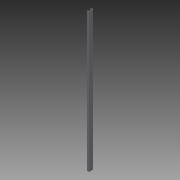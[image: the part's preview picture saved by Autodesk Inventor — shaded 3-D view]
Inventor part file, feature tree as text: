
AUTODESK INVENTOR PART (.ipt)
format: ipt  version: 2013 (Build 170138000, 138)  size: 72,192 bytes
history: native  units: in
note: dims shown in document units (in); Inventor stores cm internally (conversion verified against a paired STEP export)
features: extrude x1, sketch x1
ambient origin geometry x8: Origin, YZ Plane, XZ Plane, XY Plane, X Axis, Y Axis, Z Axis, Center Point
bodies: Solid1 (feature_tree)
feature tree (2):
  extrude  "Extrusion1"  Depth=2.0in
  sketch  "Sketch1"  dims[d0=1.0in d1=2.0in d2=0.125in d3=0.125in d4=72.0in d5=0.0in]
